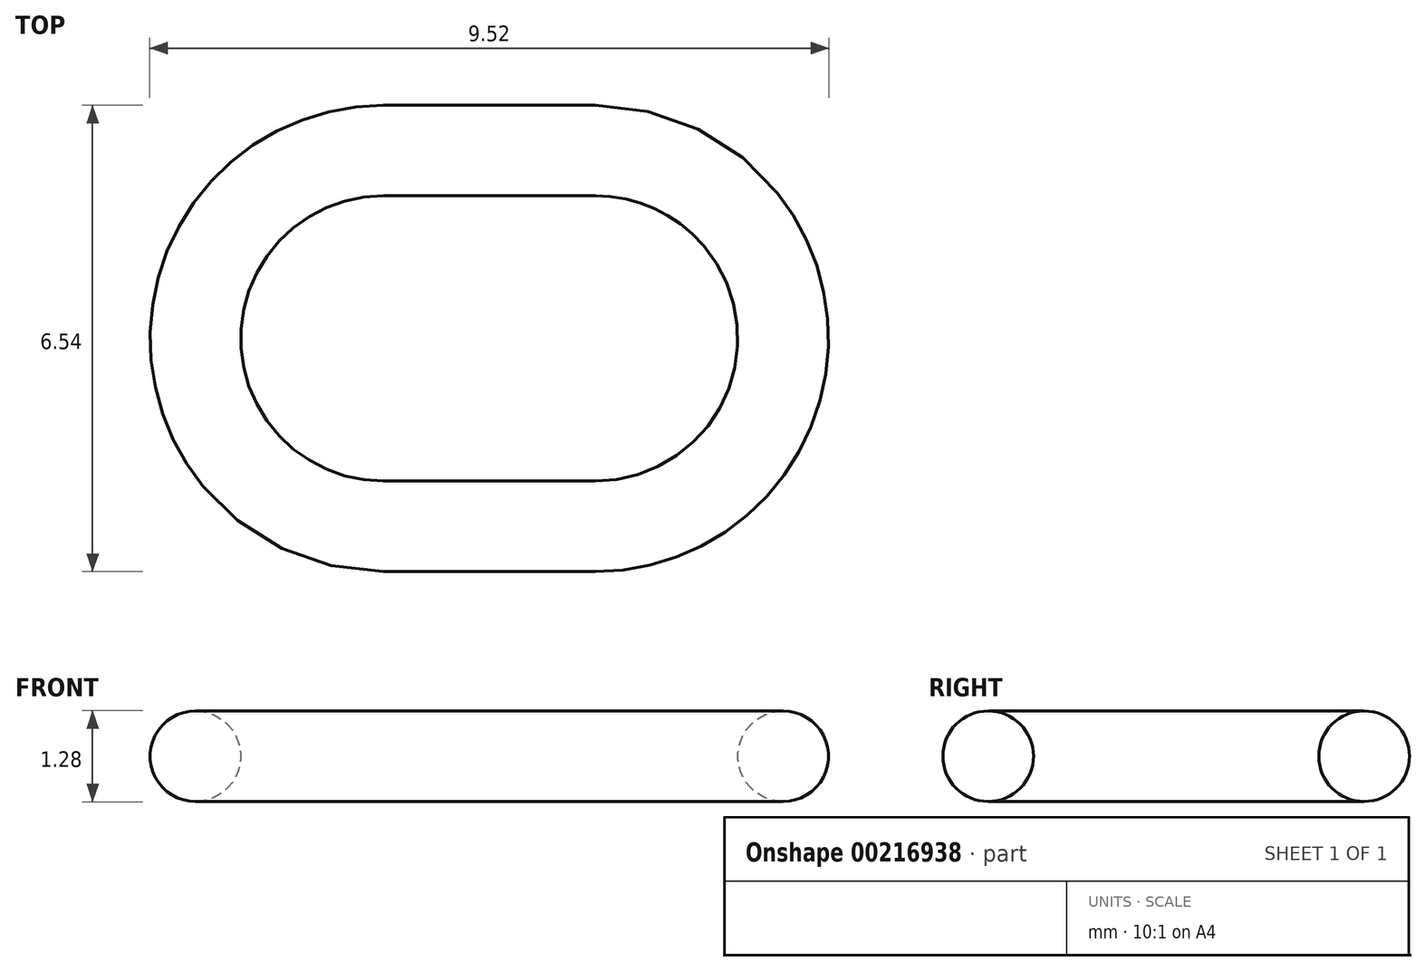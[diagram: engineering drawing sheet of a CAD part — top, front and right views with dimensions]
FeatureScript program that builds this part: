
annotation { "Feature Type Name" : "Feature", "Feature Type Description" : "" }
export const myFeature = defineFeature(function(context is Context, id is Id, definition is map)
    precondition{}
    {
        {
            var Q0;
            Q0=qCreatedBy(makeId("Top.planeOp"),FACE);
            var sketch = newSketch(context, id + "F0", { "sketchPlane" : qUnion([Q0])});
            skLineSegment(sketch, "E0", {"start": v(-1.48, 2) * mm, "end": v(1.48, 2) * mm, "construction": true});
            skLineSegment(sketch, "E1", {"start": v(-1.48, -2) * mm, "end": v(1.48, -2) * mm, "construction": true});
            skArc(sketch, "E2", {"start": v(1.48, -2) * mm, "mid": v(3.49, 0) * mm, "end": v(1.48, 2) * mm, "construction": true});
            skArc(sketch, "E3", {"start": v(-1.48, 2) * mm, "mid": v(-3.49, 0) * mm, "end": v(-1.48, -2) * mm, "construction": true});
            skLineSegment(sketch, "E4", {"start": v(0, 2) * mm, "end": v(0, -2) * mm, "construction": true});
            skLineSegment(sketch, "E5", {"start": v(-3.48, 0) * mm, "end": v(3.48, 0) * mm, "construction": true});
            skArc(sketch, "E6.0", {"start": v(-1.48, 2.64) * mm, "mid": v(-4.12, 0) * mm, "end": v(-1.48, -2.64) * mm});
            skLineSegment(sketch, "E6.1", {"start": v(-1.48, 2.64) * mm, "end": v(1.48, 2.64) * mm});
            skArc(sketch, "E6.2", {"start": v(1.48, -2.64) * mm, "mid": v(4.12, 0) * mm, "end": v(1.48, 2.64) * mm});
            skLineSegment(sketch, "E6.3", {"start": v(-1.48, -2.64) * mm, "end": v(1.48, -2.64) * mm});
            skSolve(sketch);
        }
        {
            var Q0;
            Q0=qCreatedBy(makeId("Right.planeOp"),FACE);
            var Q1;
            Q1=sQuery(id+"F0.wireOp",VERTEX,"E6.1.start");
            cPlane(context, id + "F1", {"entities" : qUnion([Q0, Q1]), "cplaneType" : CPlaneType.PLANE_POINT, "offset" : 25 * mm, "width" : 150 * mm, "height" : 150 * mm});
        }
        {
            var Q0;
            Q0=qCreatedBy(id+"F1.planeOp",FACE);
            var sketch = newSketch(context, id + "F2", { "sketchPlane" : qUnion([Q0])});
            skCircle(sketch, "E7", {"center": v(2.64, 0) * mm, "radius": 0.64 * mm});
            skSolve(sketch);
        }
        {
            var Q0;
            Q0 = qSketchRegion(id + "F2", true);
            var Q1;
            Q1 = qConstructionFilter(qBodyType(qCreatedBy(id + "F0" ,EDGE), BodyType.WIRE), ConstructionObject.NO);
            sweep(context, id + "F3", {"profiles" : qUnion([Q0]), "path" : qUnion([Q1])});
        }
    });
